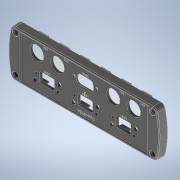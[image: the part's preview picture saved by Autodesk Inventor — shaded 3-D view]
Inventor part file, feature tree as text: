
AUTODESK INVENTOR PART (.ipt)
format: ipt  version: 2021 (Build 250183000, 183)  size: 1,080,320 bytes
history: native  units: mm
features: sketch x10, extrude x9, fillet x3, chamfer x3, plane x2, mirror x1, hole x1, projected_geometry x1, other x1
ambient origin geometry x8: Origin, YZ Plane, XZ Plane, XY Plane, X Axis, Y Axis, Z Axis, Center Point
bodies: Solid1 (feature_tree)
feature tree (31):
  extrude  "Extrusion1"  TaperAngle=0.0deg  [1 undecoded]
  fillet  "Fillet1"  Radius=6.9mm
  plane  "Work Plane1"
  extrude  "Extrusion4"  [1 undecoded]
  chamfer  "Chamfer2"  [1 undecoded]
  mirror  "Mirror1"
  plane  "Work Plane2"
  extrude  "Extrusion6"  Depth=0.2mm
  extrude  "Extrusion7"  Depth=1.0mm
  extrude  "Extrusion9"  Depth=1.0mm
  fillet  "Fillet3"  Radius=5.23mm
  hole  "Hole1"  [1 undecoded]
  extrude  "Extrusion10"  TaperAngle=0.0deg  [1 undecoded]
  extrude  "Extrusion11"  Depth=1.0mm
  extrude  "Extrusion12"  Depth=1.0mm
  fillet  "Fillet4"  Radius=5.225mm
  chamfer  "Chamfer4"  Distance=6.9mm
  chamfer  "Chamfer5"  Distance=10.075mm
  extrude  "Extrusion13"  Depth=1.0mm
  sketch  "Sketch20"  dims[d54=10.46mm d56=3.3mm d57=12.495mm d58=5.23mm d59=4.77mm d60=0.0mm d61=0.0mm d63=3.72mm d64=9.51mm d65=4.85mm d66=4.85mm d67=27.0mm d68=9.0mm d69=3.3mm d70=3.3mm d71=24.0mm d72=16.55mm d73=11.55mm d74=6.35mm d75=1.85mm d76=5.225mm d77=6.9mm d78=10.075mm d79=10.075mm d80=42.584mm d82=7.0mm d83=10.0mm d84=0.0mm d101=10.075mm d102=4.85mm d103=4.85mm d104=27.0mm d105=9.0mm d106=3.3mm d107=3.3mm d108=24.0mm d109=16.55mm d110=11.55mm d111=6.35mm d112=1.85mm d113=5.225mm d114=10.075mm d115=12.0mm d116=6.9mm d117=42.584mm d118=7.0mm d119=7.0mm d122=12.0mm d123=41.0mm d124=2.0mm d125=0.0mm d126=2.0mm d127=3.25mm d128=6.0mm d129=6.25mm d130=2.0mm d131=90.0deg d132=8.0mm d133=20.594885mm d134=10.0mm d135=0.0mm d136=10.0mm d137=0.0mm d138=0.2mm d139=0.0mm d140=3.0mm d141=0.2mm d142=2.0mm d143=45.0deg d144=0.2mm d145=2.0mm d146=45.0deg d147=10.0mm d148=0.0mm d149=8.0mm d150=12.5mm d151=8.0mm d152=12.5mm d153=12.5mm d154=8.0mm d155=8.0mm d156=12.5mm d157=4.5mm d160=4.5mm d161=1.0mm d164=1.0mm d165=1.0mm d166=2.25mm d167=28.699852mm d169=20.0mm d171=42.584mm d172=10.0mm d174=10.0mm d176=7.0mm d177=7.0mm d178=7.0mm d179=1.0mm d180=4.5mm]
  sketch  "Sketch1"  dims[d3=9.0mm d15=0.0mm d16=0.0mm d21=6.9mm]
  sketch  "Sketch5"  dims[d23=1.35mm d26=-1.5mm]
  sketch  "Sketch8"  dims[d40=15.4mm]
  sketch  "Sketch14"  dims[d41=11.5mm]
  sketch  "Sketch15"  dims[d42=54.0mm]
  sketch  "Sketch16"  dims[d43=15.4mm]
  projected_geometry  "Projected Loop5"
  sketch  "Sketch17"  dims[d44=0.0mm]
  sketch  "Sketch18"  dims[d45=31.0mm d46=0.0mm d47=0.0mm]
  sketch  "Sketch19"  dims[d48=0.2mm d49=2.0mm d50=45.0deg d53=1.745329mm]
  other  "1009799_3D"
note: 5 required parameter values undecoded (feature->parameter linkage not recoverable at this tier; creation-order binding heuristic only, values carry confidence <= 0.55)
